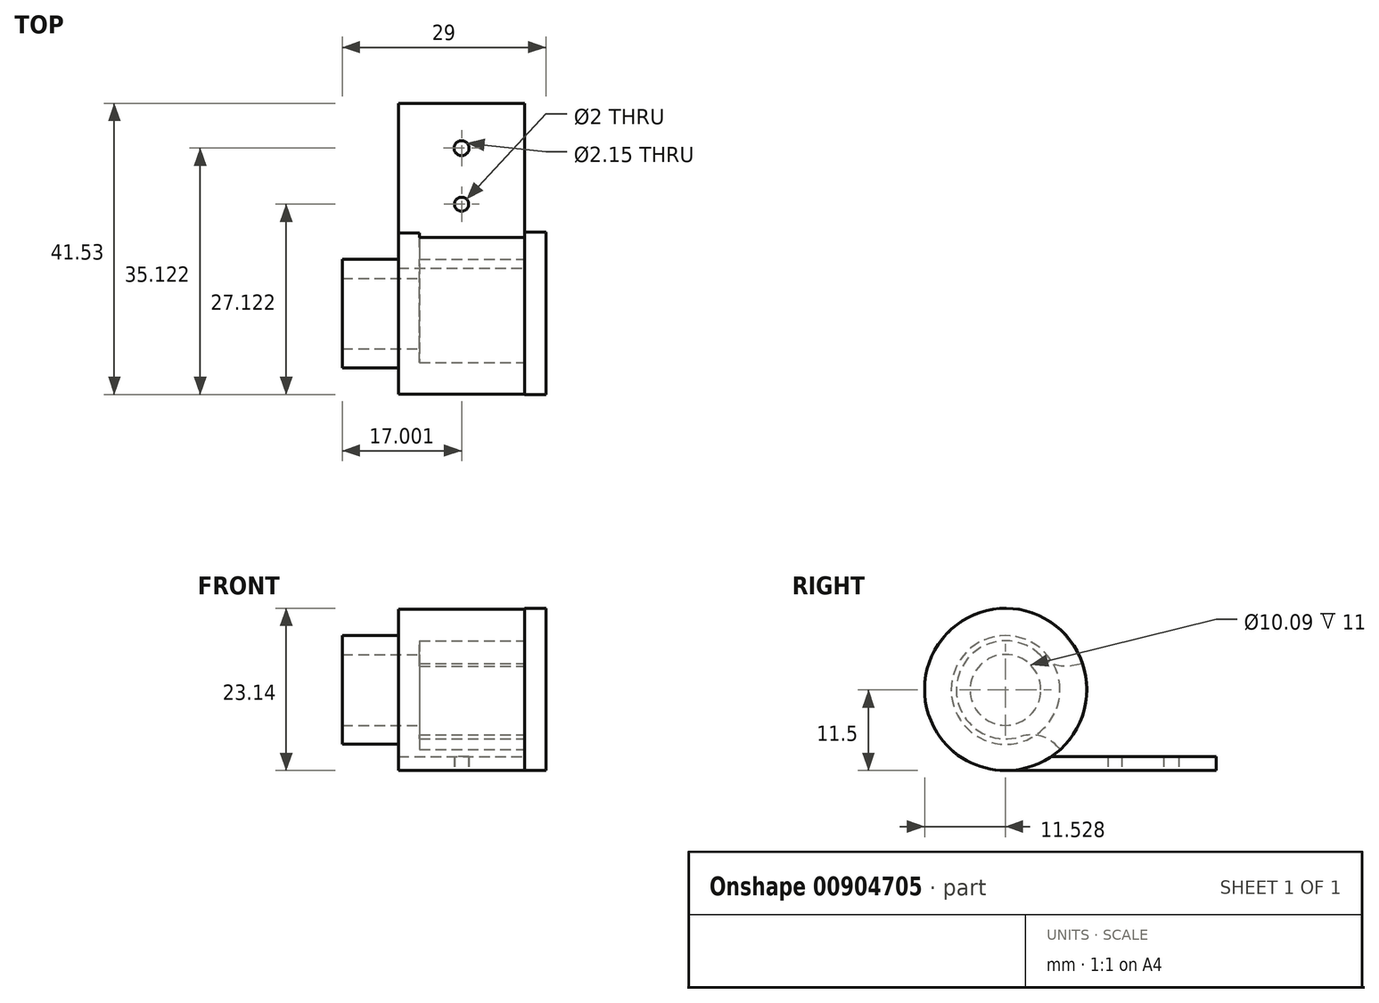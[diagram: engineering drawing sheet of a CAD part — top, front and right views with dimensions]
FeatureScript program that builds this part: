
annotation { "Feature Type Name" : "Feature", "Feature Type Description" : "" }
export const myFeature = defineFeature(function(context is Context, id is Id, definition is map)
    precondition{}
    {
        {
            var Q0;
            Q0=qCreatedBy(makeId("Top.planeOp"),FACE);
            var sketch = newSketch(context, id + "F0", { "sketchPlane" : qUnion([Q0])});
            skLineSegment(sketch, "E0.bottom", {"start": v(-29.59, -43.2) * mm, "end": v(-11.59, -43.2) * mm});
            skLineSegment(sketch, "E0.top", {"start": v(-29.59, -23.2) * mm, "end": v(-11.59, -23.2) * mm});
            skLineSegment(sketch, "E0.left", {"start": v(-29.59, -43.2) * mm, "end": v(-29.59, -23.2) * mm});
            skLineSegment(sketch, "E0.right", {"start": v(-11.59, -43.2) * mm, "end": v(-11.59, -23.2) * mm});
            skLineSegment(sketch, "E1", {"start": v(-20.59, -43.2) * mm, "end": v(-20.59, 55.19) * mm, "construction": true});
            skCircle(sketch, "E2", {"center": v(-20.59, -37.6) * mm, "radius": 1 * mm});
            skCircle(sketch, "E3", {"center": v(-20.59, -29.6) * mm, "radius": 1.07 * mm});
            skSolve(sketch);
        }
        {
            var Q0;
            Q0=makeQuery(id+"F0.imprint","IMPRINT",FACE,{"disambiguationData":[TD([[makeQuery(id+"F0.imprint","IMPRINT",EDGE,{"derivedFrom":sQuery(id+"F0.wireOp",EDGE,"E0.bottom")}),1.0]])]});
            extrude(context, id + "F1", {"entities" : qUnion([Q0]), "depth" : 2 * mm, "offsetDistance" : 25 * mm});
        }
        {
            var Q0;
            Q0=makeQuery(id+"F1.opExtrude","SWEPT_FACE",FACE,{"disambiguationData":[OSD([sQuery(id+"F0.wireOp",EDGE,"E0.right")])]});
            var sketch = newSketch(context, id + "F2", { "sketchPlane" : qUnion([Q0])});
            skArc(sketch, "E4", {"start": v(-42.32, 15.23) * mm, "mid": v(-64.34, 14.35) * mm, "end": v(-45.45, 3) * mm});
            skLineSegment(sketch, "E5", {"start": v(-58.2, 33.89) * mm, "end": v(-58.2, -8.19) * mm, "construction": true});
            skLineSegment(sketch, "E6", {"start": v(-53.2, 0) * mm, "end": v(-43.2, 0) * mm});
            skLineSegment(sketch, "E7", {"start": v(-43.2, 2) * mm, "end": v(-46.72, 2) * mm});
            skArc(sketch, "E8", {"start": v(-46.85, 14.43) * mm, "mid": v(-60.09, 12.77) * mm, "end": v(-48.3, 6.5) * mm});
            skLineSegment(sketch, "E9", {"start": v(-48.3, 6.5) * mm, "end": v(-45.45, 3) * mm});
            skLineSegment(sketch, "E10", {"start": v(-46.85, 14.43) * mm, "end": v(-42.32, 15.23) * mm});
            skSolve(sketch);
        }
        {
            var Q0;
            Q0=makeQuery(id+"F2.imprint","IMPRINT",FACE,{"disambiguationData":[TD([[makeQuery(id+"F2.imprint","IMPRINT",EDGE,{"derivedFrom":sQuery(id+"F2.wireOp",EDGE,"E8")}),-1.0]])]});
            var Q1;
            {var subQ0=sQuery(id+"F2.wireOp",EDGE,"E6");Q1=makeQuery(id+"F2.imprint","IMPRINT",FACE,{"disambiguationData":[TD([[makeQuery(id+"F2.imprint","IMPRINT",EDGE,{"derivedFrom":subQ0}),1.0]])]});}
            extrude(context, id + "F3", {"entities" : qUnion([Q0, Q1]), "operationType" : NewBodyOperationType.ADD, "oppositeDirection" : true, "depth" : 18 * mm, "offsetDistance" : 25 * mm});
        }
        {
            var Q0;
            Q0=makeQuery(id+"F3.opExtrude","SWEPT_EDGE",EDGE,{"disambiguationData":[OSD([sQuery(id+"F2.wireOp",EDGE,"E8"),sQuery(id+"F2.wireOp",EDGE,"E9")])]});
            var Q1;
            Q1=makeQuery(id+"F3.opExtrude","SWEPT_EDGE",EDGE,{"disambiguationData":[OSD([sQuery(id+"F2.wireOp",EDGE,"E8"),sQuery(id+"F2.wireOp",EDGE,"E10")])]});
            fillet(context, id + "F4", {"entities" : qUnion([Q0, Q1]), "radius" : 5 * mm, "tangentPropagation" : true, "allowEdgeOverflow" : false});
        }
        {
            var Q0;
            {var subQ0=sQuery(id+"F0.wireOp",EDGE,"E0.right");Q0=makeQuery(id+"F3.boolean.opBoolean","MERGE",FACE,{"derivedFrom":[makeQuery(id+"F1.opExtrude","SWEPT_FACE",FACE,{"disambiguationData":[OSD([subQ0])]}),makeQuery(id+"F3.opExtrude","CAP_FACE",FACE,{"disambiguationData":[OSD([sQuery(id+"F0.wireOp",EDGE,"E0.bottom"),subQ0,sQuery(id+"F2.wireOp",EDGE,"E4"),sQuery(id+"F2.wireOp",EDGE,"E6"),sQuery(id+"F2.wireOp",EDGE,"E7"),sQuery(id+"F2.wireOp",EDGE,"E8"),sQuery(id+"F2.wireOp",EDGE,"E9"),sQuery(id+"F2.wireOp",EDGE,"E10")])],"isStart":true})]});}
            var sketch = newSketch(context, id + "F5", { "sketchPlane" : qUnion([Q0])});
            skSolve(sketch);
        }
        {
            var Q0;
            Q0=makeQuery(id+"F3.boolean.opBoolean","MERGE",FACE,{"derivedFrom":[makeQuery(id+"F1.opExtrude","SWEPT_FACE",FACE,{"disambiguationData":[OSD([sQuery(id+"F0.wireOp",EDGE,"E0.left")])]}),makeQuery(id+"F3.opExtrude","CAP_FACE",FACE,{"disambiguationData":[OSD([sQuery(id+"F0.wireOp",EDGE,"E0.bottom"),sQuery(id+"F0.wireOp",EDGE,"E0.right"),sQuery(id+"F2.wireOp",EDGE,"E4"),sQuery(id+"F2.wireOp",EDGE,"E6"),sQuery(id+"F2.wireOp",EDGE,"E7"),sQuery(id+"F2.wireOp",EDGE,"E8"),sQuery(id+"F2.wireOp",EDGE,"E9"),sQuery(id+"F2.wireOp",EDGE,"E10")])],"isStart":false})]});
            var sketch = newSketch(context, id + "F6", { "sketchPlane" : qUnion([Q0])});
            skArc(sketch, "E11.0", {"start": v(42.32, 15.23) * mm, "mid": v(64.34, 14.35) * mm, "end": v(45.45, 3) * mm});
            skCircle(sketch, "E12", {"center": v(53.2, 11.5) * mm, "radius": 11.5 * mm});
            skSolve(sketch);
        }
        {
            var Q0;
            {var subQ0=sQuery(id+"F6.wireOp",EDGE,"E12");var subQ1=sQuery(id+"F2.wireOp",EDGE,"E10");var subQ9=makeQuery(id+"F3.opExtrude","CAP_EDGE",EDGE,{"disambiguationData":[OSD([subQ1])],"isStart":false});var subQ13=makeQuery(id+"F6.imprint","INTERSECT",VERTEX,{"derivedFrom":[subQ9,subQ0]});Q0=makeQuery(id+"F6.imprint","IMPRINT",FACE,{"disambiguationData":[TD([[makeQuery(id+"F6.imprint","IMPRINT",EDGE,{"disambiguationData":[TD([[subQ13,-1.0]])],"derivedFrom":subQ0}),1.0]])]});}
            var Q1;
            {var subQ0=sQuery(id+"F6.wireOp",EDGE,"E12");var subQ1=sQuery(id+"F2.wireOp",EDGE,"E10");var subQ11=makeQuery(id+"F3.opExtrude","CAP_EDGE",EDGE,{"disambiguationData":[OSD([subQ1])],"isStart":false});var subQ13=makeQuery(id+"F6.imprint","INTERSECT",VERTEX,{"derivedFrom":[subQ11,subQ0]});Q1=makeQuery(id+"F6.imprint","IMPRINT",FACE,{"disambiguationData":[TD([[makeQuery(id+"F6.imprint","IMPRINT",EDGE,{"disambiguationData":[TD([[subQ13,1.0]])],"derivedFrom":subQ0}),1.0]])]});}
            extrude(context, id + "F7", {"entities" : qUnion([Q0, Q1]), "operationType" : NewBodyOperationType.ADD, "oppositeDirection" : true, "depth" : 3 * mm, "offsetDistance" : 25 * mm});
        }
        {
            var Q0;
            {var subQ0=sQuery(id+"F2.wireOp",EDGE,"E10");var subQ1=sQuery(id+"F2.wireOp",EDGE,"E9");var subQ2=sQuery(id+"F2.wireOp",EDGE,"E8");var subQ3=sQuery(id+"F2.wireOp",EDGE,"E7");var subQ4=sQuery(id+"F2.wireOp",EDGE,"E6");var subQ5=sQuery(id+"F2.wireOp",EDGE,"E4");var subQ6=sQuery(id+"F0.wireOp",EDGE,"E0.right");var subQ7=sQuery(id+"F0.wireOp",EDGE,"E0.left");var subQ8=sQuery(id+"F0.wireOp",EDGE,"E0.bottom");Q0=makeQuery(id+"F7.boolean.opBoolean","MERGE",FACE,{"derivedFrom":[makeQuery(id+"F3.boolean.opBoolean","MERGE",FACE,{"derivedFrom":[makeQuery(id+"F1.opExtrude","SWEPT_FACE",FACE,{"disambiguationData":[OSD([subQ7])]}),makeQuery(id+"F3.opExtrude","CAP_FACE",FACE,{"disambiguationData":[OSD([subQ8,subQ6,subQ5,subQ4,subQ3,subQ2,subQ1,subQ0])],"isStart":false})]}),makeQuery(id+"F7.opExtrude","CAP_FACE",FACE,{"disambiguationData":[OSD([subQ8,subQ7,subQ6,subQ5,subQ4,subQ3,subQ2,subQ1,subQ0,sQuery(id+"F6.wireOp",EDGE,"E12")])],"isStart":true})]});}
            var sketch = newSketch(context, id + "F8", { "sketchPlane" : qUnion([Q0])});
            skCircle(sketch, "E13", {"center": v(53.2, 11.5) * mm, "radius": 5.04 * mm});
            skCircle(sketch, "E14", {"center": v(53.2, 11.5) * mm, "radius": 7.75 * mm});
            skSolve(sketch);
        }
        {
            var Q0;
            Q0=makeQuery(id+"F8.imprint","IMPRINT",FACE,{"disambiguationData":[TD([[makeQuery(id+"F8.imprint","IMPRINT",EDGE,{"derivedFrom":sQuery(id+"F8.wireOp",EDGE,"E13")}),-1.0]])]});
            extrude(context, id + "F9", {"entities" : qUnion([Q0]), "operationType" : NewBodyOperationType.ADD, "depth" : 8 * mm, "offsetDistance" : 25 * mm});
        }
        {
            var Q0;
            {var subQ0=sQuery(id+"F2.wireOp",EDGE,"E10");var subQ1=sQuery(id+"F2.wireOp",EDGE,"E9");var subQ2=sQuery(id+"F2.wireOp",EDGE,"E8");var subQ3=sQuery(id+"F2.wireOp",EDGE,"E7");var subQ4=sQuery(id+"F2.wireOp",EDGE,"E6");var subQ5=sQuery(id+"F2.wireOp",EDGE,"E4");var subQ6=sQuery(id+"F0.wireOp",EDGE,"E0.right");var subQ7=sQuery(id+"F0.wireOp",EDGE,"E0.left");var subQ8=sQuery(id+"F0.wireOp",EDGE,"E0.bottom");Q0=makeQuery(id+"F9.boolean.opBoolean","SPLIT",FACE,{"disambiguationData":[TD([makeQuery(id+"F9.opExtrude","SWEPT_FACE",FACE,{"disambiguationData":[OSD([sQuery(id+"F8.wireOp",EDGE,"E13")])]})])],"derivedFrom":makeQuery(id+"F7.boolean.opBoolean","MERGE",FACE,{"derivedFrom":[makeQuery(id+"F3.boolean.opBoolean","MERGE",FACE,{"derivedFrom":[makeQuery(id+"F1.opExtrude","SWEPT_FACE",FACE,{"disambiguationData":[OSD([subQ7])]}),makeQuery(id+"F3.opExtrude","CAP_FACE",FACE,{"disambiguationData":[OSD([subQ8,subQ6,subQ5,subQ4,subQ3,subQ2,subQ1,subQ0])],"isStart":false})]}),makeQuery(id+"F7.opExtrude","CAP_FACE",FACE,{"disambiguationData":[OSD([subQ8,subQ7,subQ6,subQ5,subQ4,subQ3,subQ2,subQ1,subQ0,sQuery(id+"F6.wireOp",EDGE,"E12")])],"isStart":true})]})});}
            extrude(context, id + "F10", {"entities" : qUnion([Q0]), "operationType" : NewBodyOperationType.REMOVE, "endBound" : BoundingType.THROUGH_ALL, "oppositeDirection" : true, "depth" : 25 * mm, "offsetDistance" : 25 * mm});
        }
        {
            var Q0;
            Q0=makeQuery(id+"F2.imprint","IMPRINT",FACE,{"disambiguationData":[TD([[makeQuery(id+"F2.imprint","IMPRINT",EDGE,{"derivedFrom":sQuery(id+"F2.wireOp",EDGE,"E8")}),-1.0]])]});
            var sketch = newSketch(context, id + "F11", { "sketchPlane" : qUnion([Q0])});
            skCircle(sketch, "E15", {"center": v(-53.17, 11.57) * mm, "radius": 11.57 * mm});
            skSolve(sketch);
        }
        {
            var Q0;
            Q0 = qSketchRegion(id + "F11", true);
            var Q1;
            {var subQ6=sQuery(id+"F2.wireOp",EDGE,"E8");Q1=makeQuery(id+"F5.imprint","IMPRINT",FACE,{"disambiguationData":[TD([[makeQuery(id+"F5.imprint","IMPRINT",EDGE,{"derivedFrom":makeQuery(id+"F3.opExtrude","CAP_EDGE",EDGE,{"disambiguationData":[OSD([subQ6])],"isStart":true})}),-1.0]])]});}
            extrude(context, id + "F12", {"entities" : qUnion([Q0, Q1]), "operationType" : NewBodyOperationType.ADD, "depth" : 3 * mm, "offsetDistance" : 25 * mm});
        }
    });
